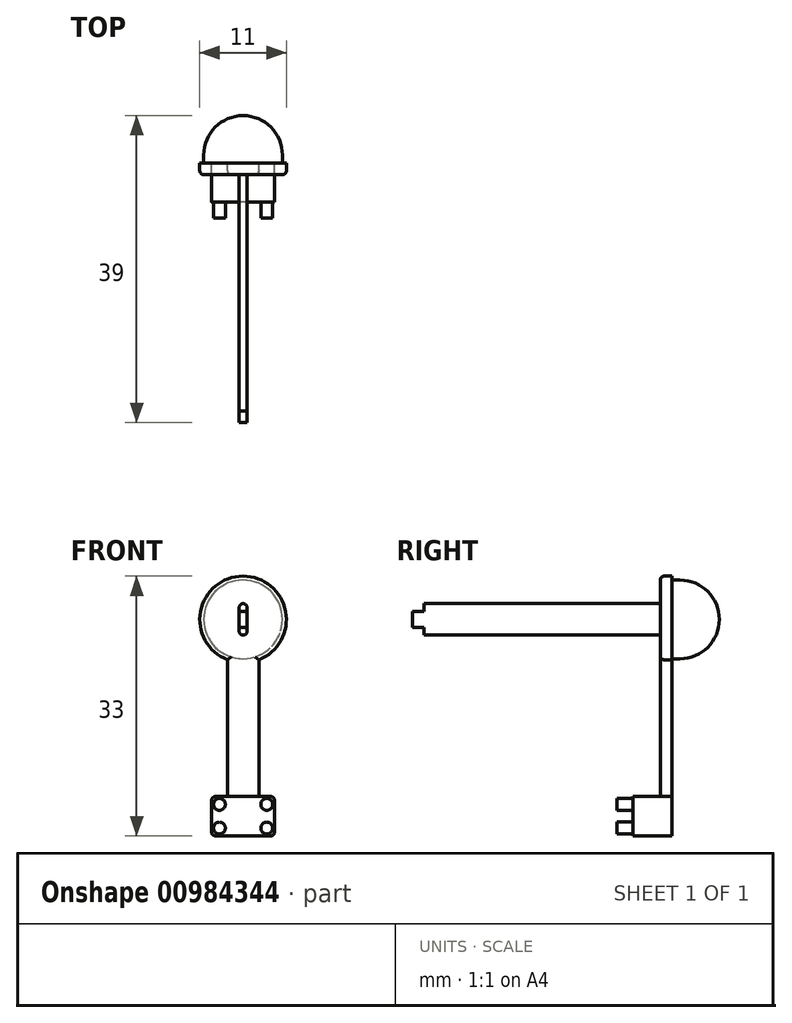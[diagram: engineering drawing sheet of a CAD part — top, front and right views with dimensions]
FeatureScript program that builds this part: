
annotation { "Feature Type Name" : "Feature", "Feature Type Description" : "" }
export const myFeature = defineFeature(function(context is Context, id is Id, definition is map)
    precondition{}
    {
        {
            var Q0;
            Q0=qCreatedBy(makeId("Front.planeOp"),FACE);
            var sketch = newSketch(context, id + "F0", { "sketchPlane" : qUnion([Q0])});
            skLineSegment(sketch, "E0.bottom", {"start": v(4, -2.5) * mm, "end": v(-4, -2.5) * mm});
            skLineSegment(sketch, "E0.top", {"start": v(4, 2.5) * mm, "end": v(-4, 2.5) * mm});
            skLineSegment(sketch, "E0.left", {"start": v(4, -2.5) * mm, "end": v(4, 2.5) * mm});
            skLineSegment(sketch, "E0.right", {"start": v(-4, -2.5) * mm, "end": v(-4, 2.5) * mm});
            skPoint(sketch, "E0.middle", {"position": v(0, 0) * mm});
            skSolve(sketch);
        }
        {
            var Q0;
            Q0=makeQuery(id+"F0.imprint","IMPRINT",FACE,{"disambiguationData":[TD([[makeQuery(id+"F0.imprint","IMPRINT",EDGE,{"derivedFrom":sQuery(id+"F0.wireOp",EDGE,"E0.bottom")}),-1.0]])]});
            var Q1;
            Q1 = qSketchRegion(id + "F4", true);
            extrude(context, id + "F1", {"entities" : qUnion([Q0, Q1]), "depth" : 5 * mm, "offsetDistance" : 25 * mm});
        }
        {
            var Q0;
            Q0=makeQuery(id+"F1.opExtrude","CAP_FACE",FACE,{"disambiguationData":[OSD([sQuery(id+"F0.wireOp",EDGE,"E0.bottom"),sQuery(id+"F0.wireOp",EDGE,"E0.top"),sQuery(id+"F0.wireOp",EDGE,"E0.left"),sQuery(id+"F0.wireOp",EDGE,"E0.right")])],"isStart":false});
            var sketch = newSketch(context, id + "F2", { "sketchPlane" : qUnion([Q0])});
            skLineSegment(sketch, "E1.bottom", {"start": v(-3, 1.5) * mm, "end": v(3, 1.5) * mm, "construction": true});
            skLineSegment(sketch, "E1.top", {"start": v(-3, -1.5) * mm, "end": v(3, -1.5) * mm, "construction": true});
            skLineSegment(sketch, "E1.left", {"start": v(-3, 1.5) * mm, "end": v(-3, -1.5) * mm, "construction": true});
            skLineSegment(sketch, "E1.right", {"start": v(3, 1.5) * mm, "end": v(3, -1.5) * mm, "construction": true});
            skCircle(sketch, "E2", {"center": v(-3, 1.5) * mm, "radius": 0.75 * mm});
            skCircle(sketch, "E3", {"center": v(3, 1.5) * mm, "radius": 0.75 * mm});
            skCircle(sketch, "E4", {"center": v(3, -1.5) * mm, "radius": 0.75 * mm});
            skCircle(sketch, "E5", {"center": v(-3, -1.5) * mm, "radius": 0.75 * mm});
            skSolve(sketch);
        }
        {
            var Q0;
            Q0=makeQuery(id+"F2.imprint","IMPRINT",FACE,{"disambiguationData":[TD([[makeQuery(id+"F2.imprint","IMPRINT",EDGE,{"derivedFrom":sQuery(id+"F2.wireOp",EDGE,"E2")}),1.0]])]});
            var Q1;
            Q1=makeQuery(id+"F2.imprint","IMPRINT",FACE,{"disambiguationData":[TD([[makeQuery(id+"F2.imprint","IMPRINT",EDGE,{"derivedFrom":sQuery(id+"F2.wireOp",EDGE,"E3")}),1.0]])]});
            var Q2;
            Q2=makeQuery(id+"F2.imprint","IMPRINT",FACE,{"disambiguationData":[TD([[makeQuery(id+"F2.imprint","IMPRINT",EDGE,{"derivedFrom":sQuery(id+"F2.wireOp",EDGE,"E5")}),1.0]])]});
            var Q3;
            Q3=makeQuery(id+"F2.imprint","IMPRINT",FACE,{"disambiguationData":[TD([[makeQuery(id+"F2.imprint","IMPRINT",EDGE,{"derivedFrom":sQuery(id+"F2.wireOp",EDGE,"E4")}),1.0]])]});
            extrude(context, id + "F3", {"entities" : qUnion([Q0, Q1, Q2, Q3]), "operationType" : NewBodyOperationType.ADD, "depth" : 2 * mm, "offsetDistance" : 25 * mm});
        }
        {
            var Q0;
            Q0=makeQuery(id+"F1.opExtrude","SWEPT_FACE",FACE,{"disambiguationData":[OSD([sQuery(id+"F0.wireOp",EDGE,"E0.top")])]});
            var sketch = newSketch(context, id + "F4", { "sketchPlane" : qUnion([Q0])});
            skLineSegment(sketch, "E6.bottom", {"start": v(2, -1.5) * mm, "end": v(-2, -1.5) * mm});
            skLineSegment(sketch, "E6.top", {"start": v(2, 0) * mm, "end": v(-2, 0) * mm});
            skLineSegment(sketch, "E6.left", {"start": v(2, -1.5) * mm, "end": v(2, 0) * mm});
            skLineSegment(sketch, "E6.right", {"start": v(-2, -1.5) * mm, "end": v(-2, 0) * mm});
            skPoint(sketch, "E6.middle", {"position": v(0, -0.75) * mm});
            skSolve(sketch);
        }
        {
            var Q0;
            Q0=makeQuery(id+"F4.imprint","IMPRINT",FACE,{"disambiguationData":[TD([[makeQuery(id+"F4.imprint","IMPRINT",EDGE,{"derivedFrom":sQuery(id+"F4.wireOp",EDGE,"E6.bottom")}),-1.0]])]});
            extrude(context, id + "F5", {"entities" : qUnion([Q0]), "operationType" : NewBodyOperationType.ADD, "depth" : 23.5 * mm, "offsetDistance" : 25 * mm});
        }
        {
            var Q0;
            Q0=makeQuery(id+"F5.opExtrude","SWEPT_FACE",FACE,{"disambiguationData":[OSD([sQuery(id+"F4.wireOp",EDGE,"E6.top")])]});
            var sketch = newSketch(context, id + "F6", { "sketchPlane" : qUnion([Q0])});
            skCircle(sketch, "E7", {"center": v(0, 25) * mm, "radius": 5.5 * mm});
            skPoint(sketch, "E7.centerSnap0", {"position": v(0, 26) * mm});
            skSolve(sketch);
        }
        {
            var Q0;
            {var subQ1=sQuery(id+"F4.wireOp",EDGE,"E6.top");var subQ6=makeQuery(id+"F5.opExtrude","CAP_EDGE",EDGE,{"disambiguationData":[OSD([subQ1])],"isStart":false});Q0=makeQuery(id+"F6.imprint","IMPRINT",FACE,{"disambiguationData":[TD([[makeQuery(id+"F6.imprint","IMPRINT",EDGE,{"derivedFrom":subQ6}),1.0]])]});}
            var Q1;
            {var subQ1=sQuery(id+"F4.wireOp",EDGE,"E6.top");var subQ6=makeQuery(id+"F5.opExtrude","CAP_EDGE",EDGE,{"disambiguationData":[OSD([subQ1])],"isStart":false});Q1=makeQuery(id+"F6.imprint","IMPRINT",FACE,{"disambiguationData":[TD([[makeQuery(id+"F6.imprint","IMPRINT",EDGE,{"derivedFrom":subQ6}),-1.0]])]});}
            extrude(context, id + "F7", {"entities" : qUnion([Q0, Q1]), "operationType" : NewBodyOperationType.ADD, "oppositeDirection" : true, "depth" : 1.5 * mm, "offsetDistance" : 25 * mm});
        }
        {
            var Q0;
            Q0=makeQuery(id+"F7.boolean.opBoolean","MERGE",FACE,{"derivedFrom":[makeQuery(id+"F5.opExtrude","SWEPT_FACE",FACE,{"disambiguationData":[OSD([sQuery(id+"F4.wireOp",EDGE,"E6.bottom")])]}),makeQuery(id+"F7.opExtrude","CAP_FACE",FACE,{"disambiguationData":[OSD([sQuery(id+"F6.wireOp",EDGE,"E7")])],"isStart":false})]});
            var sketch = newSketch(context, id + "F8", { "sketchPlane" : qUnion([Q0])});
            skLineSegment(sketch, "E8.bottom", {"start": v(0.5, 23) * mm, "end": v(-0.5, 23) * mm});
            skLineSegment(sketch, "E8.top", {"start": v(0.5, 27) * mm, "end": v(-0.5, 27) * mm});
            skLineSegment(sketch, "E8.left", {"start": v(0.5, 23) * mm, "end": v(0.5, 27) * mm});
            skLineSegment(sketch, "E8.right", {"start": v(-0.5, 23) * mm, "end": v(-0.5, 27) * mm});
            skPoint(sketch, "E8.middle", {"position": v(0, 25) * mm});
            skSolve(sketch);
        }
        {
            var Q0;
            Q0=makeQuery(id+"F8.imprint","IMPRINT",FACE,{"disambiguationData":[TD([[makeQuery(id+"F8.imprint","IMPRINT",EDGE,{"derivedFrom":sQuery(id+"F8.wireOp",EDGE,"E8.bottom")}),-1.0]])]});
            extrude(context, id + "F9", {"entities" : qUnion([Q0]), "operationType" : NewBodyOperationType.ADD, "depth" : 30 * mm, "offsetDistance" : 25 * mm});
        }
        {
            var Q0;
            Q0=makeQuery(id+"F9.opExtrude","CAP_FACE",FACE,{"disambiguationData":[OSD([sQuery(id+"F8.wireOp",EDGE,"E8.bottom"),sQuery(id+"F8.wireOp",EDGE,"E8.top"),sQuery(id+"F8.wireOp",EDGE,"E8.left"),sQuery(id+"F8.wireOp",EDGE,"E8.right")])],"isStart":false});
            var sketch = newSketch(context, id + "F10", { "sketchPlane" : qUnion([Q0])});
            skLineSegment(sketch, "E9.bottom", {"start": v(0.5, 24) * mm, "end": v(-0.5, 24) * mm});
            skLineSegment(sketch, "E9.top", {"start": v(0.5, 26) * mm, "end": v(-0.5, 26) * mm});
            skLineSegment(sketch, "E9.left", {"start": v(0.5, 24) * mm, "end": v(0.5, 26) * mm});
            skLineSegment(sketch, "E9.right", {"start": v(-0.5, 24) * mm, "end": v(-0.5, 26) * mm});
            skPoint(sketch, "E9.middle", {"position": v(0, 25) * mm});
            skPoint(sketch, "E9.middle.positionSnap0", {"position": v(-0.5, 25) * mm});
            skPoint(sketch, "E9.centerSnap0", {"position": v(-0.5, 25) * mm});
            skSolve(sketch);
        }
        {
            var Q0;
            Q0=makeQuery(id+"F10.imprint","IMPRINT",FACE,{"disambiguationData":[TD([[makeQuery(id+"F10.imprint","IMPRINT",EDGE,{"derivedFrom":sQuery(id+"F10.wireOp",EDGE,"E9.bottom")}),-1.0]])]});
            extrude(context, id + "F11", {"entities" : qUnion([Q0]), "operationType" : NewBodyOperationType.ADD, "depth" : 1.5 * mm, "offsetDistance" : 25 * mm});
        }
        {
            var Q0;
            Q0=makeQuery(id+"F7.boolean.opBoolean","MERGE",FACE,{"derivedFrom":[makeQuery(id+"F5.boolean.opBoolean","MERGE",FACE,{"derivedFrom":[makeQuery(id+"F1.opExtrude","CAP_FACE",FACE,{"disambiguationData":[OSD([sQuery(id+"F0.wireOp",EDGE,"E0.bottom"),sQuery(id+"F0.wireOp",EDGE,"E0.top"),sQuery(id+"F0.wireOp",EDGE,"E0.left"),sQuery(id+"F0.wireOp",EDGE,"E0.right")])],"isStart":true}),makeQuery(id+"F5.opExtrude","SWEPT_FACE",FACE,{"disambiguationData":[OSD([sQuery(id+"F4.wireOp",EDGE,"E6.top")])]})]}),makeQuery(id+"F7.opExtrude","CAP_FACE",FACE,{"disambiguationData":[OSD([sQuery(id+"F6.wireOp",EDGE,"E7")])],"isStart":true})]});
            var sketch = newSketch(context, id + "F12", { "sketchPlane" : qUnion([Q0])});
            skCircle(sketch, "E10", {"center": v(0, 25) * mm, "radius": 5 * mm});
            skSolve(sketch);
        }
        {
            var Q0;
            Q0=makeQuery(id+"F12.imprint","IMPRINT",FACE,{"disambiguationData":[TD([[makeQuery(id+"F12.imprint","IMPRINT",EDGE,{"derivedFrom":sQuery(id+"F12.wireOp",EDGE,"E10")}),1.0]])]});
            extrude(context, id + "F13", {"entities" : qUnion([Q0]), "operationType" : NewBodyOperationType.ADD, "depth" : 1 * mm, "offsetDistance" : 25 * mm});
        }
        {
            var Q0;
            Q0=makeQuery(id+"F13.opExtrude","CAP_FACE",FACE,{"disambiguationData":[OSD([sQuery(id+"F12.wireOp",EDGE,"E10")])],"isStart":false});
            var sketch = newSketch(context, id + "F14", { "sketchPlane" : qUnion([Q0])});
            skArc(sketch, "E11", {"start": v(0, 30) * mm, "mid": v(-5, 25) * mm, "end": v(0, 20) * mm});
            skPoint(sketch, "E12", {"position": v(0, 30) * mm});
            skPoint(sketch, "E13", {"position": v(0, 20) * mm});
            skLineSegment(sketch, "E14", {"start": v(0, 30) * mm, "end": v(0, 20) * mm});
            skSolve(sketch);
        }
        {
            var Q0;
            Q0=makeQuery(id+"F14.imprint","IMPRINT",FACE,{"disambiguationData":[TD([[makeQuery(id+"F14.imprint","IMPRINT",EDGE,{"derivedFrom":sQuery(id+"F14.wireOp",EDGE,"E11")}),1.0]])]});
            var Q1;
            Q1=sQuery(id+"F14.wireOp",EDGE,"E14");
            revolve(context, id + "F15", {"operationType" : NewBodyOperationType.ADD, "surfaceOperationType" : NewSurfaceOperationType.NEW, "entities" : qUnion([Q0]), "axis" : qUnion([Q1]), "revolveType" : RevolveType.ONE_DIRECTION, "oppositeDirection" : true, "angle" : 180 * degree});
        }
        {
            var Q0;
            Q0=makeQuery(id+"F9.opExtrude","SWEPT_EDGE",EDGE,{"disambiguationData":[OSD([sQuery(id+"F8.wireOp",EDGE,"E8.top"),sQuery(id+"F8.wireOp",EDGE,"E8.right")])]});
            var Q1;
            Q1=makeQuery(id+"F9.opExtrude","SWEPT_EDGE",EDGE,{"disambiguationData":[OSD([sQuery(id+"F8.wireOp",EDGE,"E8.top"),sQuery(id+"F8.wireOp",EDGE,"E8.left")])]});
            var Q2;
            Q2=makeQuery(id+"F9.opExtrude","SWEPT_EDGE",EDGE,{"disambiguationData":[OSD([sQuery(id+"F8.wireOp",EDGE,"E8.bottom"),sQuery(id+"F8.wireOp",EDGE,"E8.left")])]});
            var Q3;
            Q3=makeQuery(id+"F9.opExtrude","SWEPT_EDGE",EDGE,{"disambiguationData":[OSD([sQuery(id+"F8.wireOp",EDGE,"E8.bottom"),sQuery(id+"F8.wireOp",EDGE,"E8.right")])]});
            fillet(context, id + "F16", {"entities" : qUnion([Q0, Q1, Q2, Q3]), "radius" : 0.5 * mm, "tangentPropagation" : true, "allowEdgeOverflow" : false});
        }
        {
            var Q0;
            Q0=makeQuery(id+"F1.opExtrude","SWEPT_EDGE",EDGE,{"disambiguationData":[OSD([sQuery(id+"F0.wireOp",EDGE,"E0.top"),sQuery(id+"F0.wireOp",EDGE,"E0.right")])]});
            var Q1;
            Q1=makeQuery(id+"F1.opExtrude","SWEPT_EDGE",EDGE,{"disambiguationData":[OSD([sQuery(id+"F0.wireOp",EDGE,"E0.bottom"),sQuery(id+"F0.wireOp",EDGE,"E0.right")])]});
            var Q2;
            Q2=makeQuery(id+"F1.opExtrude","SWEPT_EDGE",EDGE,{"disambiguationData":[OSD([sQuery(id+"F0.wireOp",EDGE,"E0.bottom"),sQuery(id+"F0.wireOp",EDGE,"E0.left")])]});
            var Q3;
            Q3=makeQuery(id+"F1.opExtrude","SWEPT_EDGE",EDGE,{"disambiguationData":[OSD([sQuery(id+"F0.wireOp",EDGE,"E0.top"),sQuery(id+"F0.wireOp",EDGE,"E0.left")])]});
            fillet(context, id + "F17", {"entities" : qUnion([Q0, Q1, Q2, Q3]), "radius" : 0.5 * mm, "tangentPropagation" : true, "allowEdgeOverflow" : false});
        }
        {
            var Q0;
            Q0=makeQuery(id+"F5.opExtrude","SWEPT_EDGE",EDGE,{"disambiguationData":[OSD([sQuery(id+"F4.wireOp",EDGE,"E6.bottom"),sQuery(id+"F4.wireOp",EDGE,"E6.right")])]});
            var Q1;
            Q1=makeQuery(id+"F5.opExtrude","SWEPT_EDGE",EDGE,{"disambiguationData":[OSD([sQuery(id+"F4.wireOp",EDGE,"E6.bottom"),sQuery(id+"F4.wireOp",EDGE,"E6.left")])]});
            var Q2;
            Q2=makeQuery(id+"F7.opExtrude","CAP_EDGE",EDGE,{"disambiguationData":[OSD([sQuery(id+"F6.wireOp",EDGE,"E7")])],"isStart":false});
            fillet(context, id + "F18", {"entities" : qUnion([Q0, Q1, Q2]), "radius" : 0.5 * mm, "tangentPropagation" : true, "allowEdgeOverflow" : false});
        }
    });
